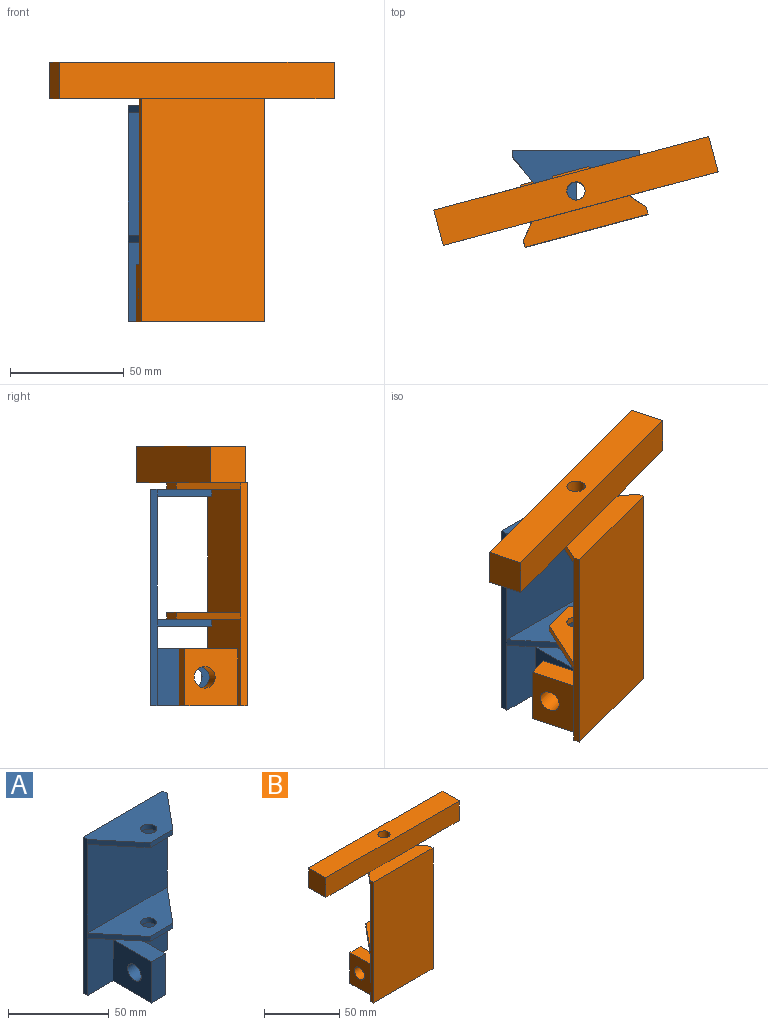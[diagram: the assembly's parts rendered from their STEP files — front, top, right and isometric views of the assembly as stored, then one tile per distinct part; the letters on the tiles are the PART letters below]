
ASSEMBLY  parts=2 mates=1
PART A: 23 faces, bbox 56x30x95 mm
  f0: plane 56x24mm, normal (0,0,-1), area 813.7mm2, adj f2,f3,f4,f15,f16
  f1: plane 56x54mm, normal (0,-1,0), area 3024mm2, adj f5,f6,f8,f13
  f2: plane 24x20mm, normal (-0.77,-0.64,0), area 93.7mm2, adj f0,f3,f5,f8
  f3: plane 16x3mm, normal (0,-1,0), area 48mm2, adj f0,f2,f4,f5
  f4: plane 24x20mm, normal (0.77,-0.64,0), area 93.7mm2, adj f0,f3,f5,f6
  f5: plane 56x24mm, normal (0,0,1), area 813.7mm2, adj f1,f2,f3,f4,f15
  f6: plane 95x3mm, normal (1,0,0), area 285mm2, adj f1,f4,f7,f9,f12,f16,f17
  f7: plane 95x56mm, normal (0,1,0), area 5320mm2, adj f6,f8,f9,f17
  f8: plane 95x3mm, normal (-1,0,0), area 285mm2, adj f1,f2,f7,f9,f10,f16,f17
  f9: plane 56x27mm, normal (0,0,1), area 981.7mm2, adj f6,f7,f8,f10,f11,f12,f14
  f10: plane 24x20mm, normal (-0.77,-0.64,0), area 93.7mm2, adj f8,f9,f11,f13
  f11: plane 16x3mm, normal (0,-1,0), area 48mm2, adj f9,f10,f12,f13
  f12: plane 24x20mm, normal (0.77,-0.64,0), area 93.7mm2, adj f6,f9,f11,f13
  f13: plane 56x24mm, normal (0,0,-1), area 813.7mm2, adj f1,f10,f11,f12,f14
  f14: cylinder r=4mm len=8mm, axis (0,0,-1), area 75.4mm2, adj f9,f13
  f15: cylinder r=4mm len=8mm, axis (0,0,-1), area 75.4mm2, adj f0,f5
  f16: plane 56x35mm, normal (0,-1,0), area 1710mm2, adj f0,f6,f8,f17,f18,f19,f20
  f17: plane 56x30mm, normal (0,0,-1), area 438mm2, adj f6,f7,f8,f16,f19,f20,f21
  f18: plane 27x10mm, normal (0,0,1), area 270mm2, adj f16,f19,f20,f21
  f19: plane 27x25mm, normal (-1,0,0), area 603.7mm2, adj f16,f17,f18,f21,f22
  f20: plane 27x25mm, normal (1,0,0), area 603.7mm2, adj f16,f17,f18,f21,f22
  f21: plane 25x10mm, normal (0,-1,0), area 250mm2, adj f17,f18,f19,f20
  f22: cylinder r=4.76mm len=10mm, axis (-1,0,0), area 299.2mm2, adj f19,f20
PART B: 31 faces, bbox 125x27x114 mm
  f0: plane 56x24mm, normal (0,0,-1), area 813.7mm2, adj f3,f4,f5,f16,f24
  f1: plane 56x10mm, normal (0,0,1), area 519.2mm2, adj f7,f8,f9,f11,f13,f19
  f2: plane 56x54mm, normal (0,1,0), area 3024mm2, adj f6,f7,f9,f14
  f3: plane 24x20mm, normal (0.77,0.64,0), area 93.7mm2, adj f0,f4,f6,f9
  f4: plane 16x3mm, normal (0,1,0), area 48mm2, adj f0,f3,f5,f6
  f5: plane 24x20mm, normal (-0.77,0.64,0), area 93.7mm2, adj f0,f4,f6,f7
  f6: plane 56x24mm, normal (0,0,1), area 813.7mm2, adj f2,f3,f4,f5,f16
  f7: plane 98x3mm, normal (-1,0,0), area 294mm2, adj f1,f2,f5,f8,f13,f24,f25
  f8: plane 98x56mm, normal (0,-1,0), area 5488mm2, adj f1,f7,f9,f25
  f9: plane 98x3mm, normal (1,0,0), area 294mm2, adj f1,f2,f3,f8,f11,f24,f25
  f10: plane 17.67x1mm, normal (0,0,1), area 16.8mm2, adj f11,f12,f13,f21
  f11: plane 24x20mm, normal (0.77,0.64,0), area 93.7mm2, adj f1,f9,f10,f12,f14,f17
  f12: plane 16x3mm, normal (0,1,0), area 48mm2, adj f10,f11,f13,f14
  f13: plane 24x20mm, normal (-0.77,0.64,0), area 93.7mm2, adj f1,f7,f10,f12,f14,f18
  f14: plane 56x24mm, normal (0,0,-1), area 813.7mm2, adj f2,f11,f12,f13,f15
  f15: cylinder r=4mm len=19mm, axis (0,0,-1), area 477.5mm2, adj f14,f23
  f16: cylinder r=4mm len=8mm, axis (0,0,-1), area 75.4mm2, adj f0,f6
  f17: plane 53.67x16mm, normal (0,0,-1), area 752mm2, adj f11,f19,f20,f21
  f18: plane 53.67x16mm, normal (0,0,-1), area 752mm2, adj f13,f19,f21,f22
  f19: plane 125x16mm, normal (0,-1,0), area 2000mm2, adj f1,f17,f18,f20,f22,f23
  f20: plane 16x16mm, normal (1,0,0), area 256mm2, adj f17,f19,f21,f23
  f21: plane 125x16mm, normal (0,1,0), area 2000mm2, adj f10,f17,f18,f20,f22,f23
  f22: plane 16x16mm, normal (-1,0,0), area 256mm2, adj f18,f19,f21,f23
  f23: plane 125x16mm, normal (0,0,1), area 1949.7mm2, adj f15,f19,f20,f21,f22
  f24: plane 56x38mm, normal (0,1,0), area 1878mm2, adj f0,f7,f9,f25,f26,f27,f28
  f25: plane 56x27mm, normal (0,0,-1), area 408mm2, adj f7,f8,f9,f24,f26,f28,f29
  f26: plane 25x24mm, normal (-1,0,0), area 528.7mm2, adj f24,f25,f27,f29,f30
  f27: plane 24x10mm, normal (0,0,1), area 240mm2, adj f24,f26,f28,f29
  f28: plane 25x24mm, normal (1,0,0), area 528.7mm2, adj f24,f25,f27,f29,f30
  f29: plane 25x10mm, normal (0,1,0), area 250mm2, adj f25,f26,f27,f28
  f30: cylinder r=4.76mm len=10mm, axis (-1,0,0), area 299.2mm2, adj f26,f28
PLACE A t=(3.66,-11.1,2.51)mm fixed
PLACE B rot(axis=(0,0,1),15deg) t=(3.66,-11.1,2.51)mm
MATE revolute A.f14 <-> B.f15  axis (0,0,1) through (3.66,-11.1,62.51)mm
